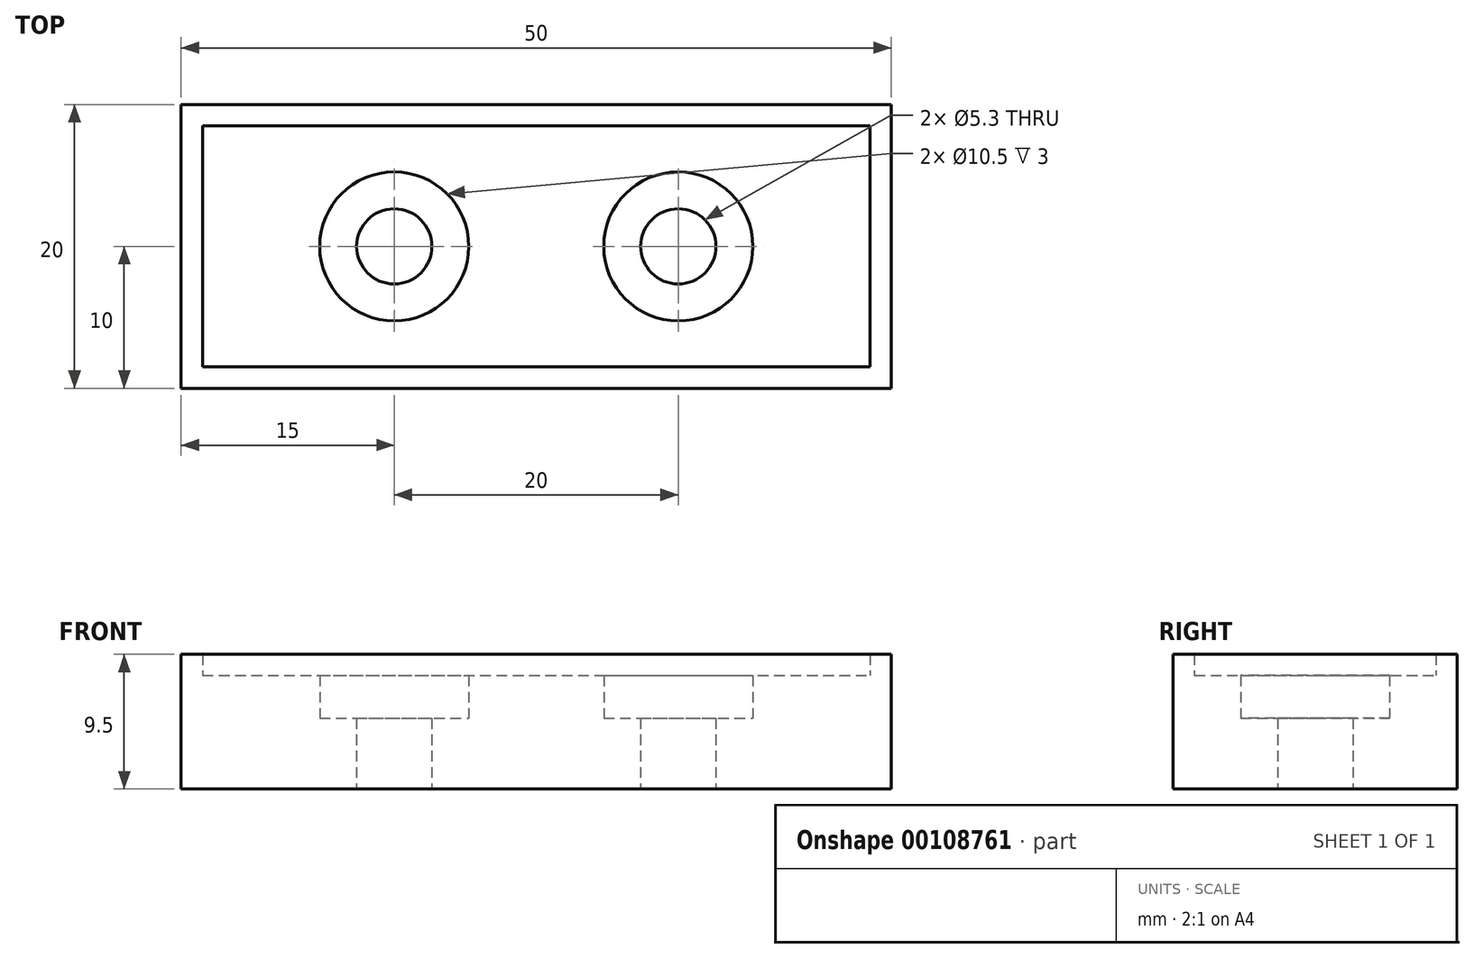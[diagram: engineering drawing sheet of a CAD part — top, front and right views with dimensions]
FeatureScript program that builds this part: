
annotation { "Feature Type Name" : "Feature", "Feature Type Description" : "" }
export const myFeature = defineFeature(function(context is Context, id is Id, definition is map)
    precondition{}
    {
        {
            var Q0;
            Q0=qCreatedBy(makeId("Top.planeOp"),FACE);
            var sketch = newSketch(context, id + "F0", { "sketchPlane" : qUnion([Q0])});
            skLineSegment(sketch, "E0.bottom", {"start": v(0, 0) * mm, "end": v(50, 0) * mm});
            skLineSegment(sketch, "E0.top", {"start": v(0, 20) * mm, "end": v(50, 20) * mm});
            skLineSegment(sketch, "E0.left", {"start": v(0, 0) * mm, "end": v(0, 20) * mm});
            skLineSegment(sketch, "E0.right", {"start": v(50, 0) * mm, "end": v(50, 20) * mm});
            skSolve(sketch);
        }
        {
            var Q0;
            Q0=makeQuery(id+"F0.imprint","IMPRINT",FACE,{"disambiguationData":[TD([[makeQuery(id+"F0.imprint","IMPRINT",EDGE,{"derivedFrom":sQuery(id+"F0.wireOp",EDGE,"E0.bottom")}),1.0]])]});
            extrude(context, id + "F1", {"entities" : qUnion([Q0]), "depth" : 8 * mm});
        }
        {
            var Q0;
            Q0=makeQuery(id+"F1.opExtrude","CAP_FACE",FACE,{"disambiguationData":[OSD([sQuery(id+"F0.wireOp",EDGE,"E0.bottom"),sQuery(id+"F0.wireOp",EDGE,"E0.top"),sQuery(id+"F0.wireOp",EDGE,"E0.left"),sQuery(id+"F0.wireOp",EDGE,"E0.right")])],"isStart":false});
            var sketch = newSketch(context, id + "F2", { "sketchPlane" : qUnion([Q0])});
            skPoint(sketch, "E1", {"position": v(15, 10) * mm});
            skPoint(sketch, "E2", {"position": v(35, 10) * mm});
            skLineSegment(sketch, "E3", {"start": v(15, 10) * mm, "end": v(0, 10) * mm, "construction": true});
            skLineSegment(sketch, "E4", {"start": v(15, 10) * mm, "end": v(35, 10) * mm, "construction": true});
            skLineSegment(sketch, "E5", {"start": v(35, 10) * mm, "end": v(50, 10) * mm, "construction": true});
            skSolve(sketch);
        }
        {
            var Q0;
            Q0=sQuery(id+"F2.wireOp",VERTEX,"E1");
            var Q1;
            Q1=sQuery(id+"F2.wireOp",VERTEX,"E2");
            var Q2;
            Q2=makeQuery(id+"F1.opExtrude","SWEPT_BODY",BODY,{"disambiguationData":[OSD([sQuery(id+"F0.wireOp",EDGE,"E0.bottom"),sQuery(id+"F0.wireOp",EDGE,"E0.top"),sQuery(id+"F0.wireOp",EDGE,"E0.left"),sQuery(id+"F0.wireOp",EDGE,"E0.right")])]});
            hole(context, id + "F3", {"style" : HoleStyle.C_BORE, "endStyle" : HoleEndStyle.THROUGH, "holeDiameter" : 5.3 * mm, "cBoreDiameter" : 10.5 * mm, "cBoreDepth" : 3 * mm, "locations" : qUnion([Q0, Q1]), "scope" : qUnion([Q2]), "isTappedThrough" : true});
        }
        {
            var Q0;
            Q0=makeQuery(id+"F1.opExtrude","CAP_FACE",FACE,{"disambiguationData":[OSD([sQuery(id+"F0.wireOp",EDGE,"E0.bottom"),sQuery(id+"F0.wireOp",EDGE,"E0.top"),sQuery(id+"F0.wireOp",EDGE,"E0.left"),sQuery(id+"F0.wireOp",EDGE,"E0.right")])],"isStart":false});
            var sketch = newSketch(context, id + "F4", { "sketchPlane" : qUnion([Q0])});
            skLineSegment(sketch, "E6.0", {"start": v(0, 20) * mm, "end": v(50, 20) * mm});
            skLineSegment(sketch, "E6.1", {"start": v(0, 0) * mm, "end": v(0, 20) * mm});
            skLineSegment(sketch, "E6.2", {"start": v(0, 0) * mm, "end": v(50, 0) * mm});
            skLineSegment(sketch, "E6.3", {"start": v(50, 0) * mm, "end": v(50, 20) * mm});
            skLineSegment(sketch, "E7.0", {"start": v(48.5, 1.5) * mm, "end": v(48.5, 18.5) * mm});
            skLineSegment(sketch, "E7.1", {"start": v(1.5, 1.5) * mm, "end": v(48.5, 1.5) * mm});
            skLineSegment(sketch, "E7.2", {"start": v(1.5, 1.5) * mm, "end": v(1.5, 18.5) * mm});
            skLineSegment(sketch, "E7.3", {"start": v(1.5, 18.5) * mm, "end": v(48.5, 18.5) * mm});
            skSolve(sketch);
        }
        {
            var Q0;
            Q0=makeQuery(id+"F4.imprint","IMPRINT",FACE,{"disambiguationData":[TD([[makeQuery(id+"F4.imprint","IMPRINT",EDGE,{"derivedFrom":sQuery(id+"F4.wireOp",EDGE,"E6.0")}),-1.0]])]});
            extrude(context, id + "F5", {"entities" : qUnion([Q0]), "operationType" : NewBodyOperationType.ADD, "depth" : 1.5 * mm});
        }
    });
